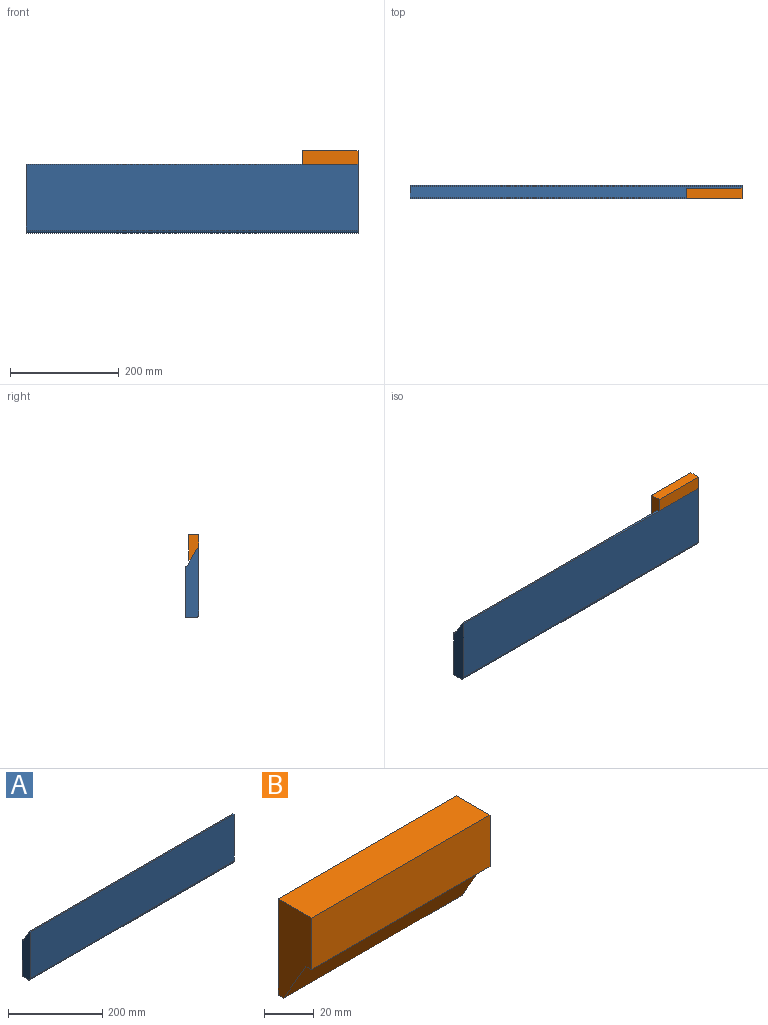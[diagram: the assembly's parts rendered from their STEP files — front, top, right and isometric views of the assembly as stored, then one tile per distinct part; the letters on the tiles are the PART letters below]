
ASSEMBLY  parts=2 mates=1
PART A: 9 faces, bbox 609.6x25.4x127 mm
  f0: plane 609.6x3.18mm, normal (0,0,1), area 1935.5mm2, adj f1,f6,f7,f8
  f1: plane 609.6x120.65mm, normal (0,-1,0), area 73548.2mm2, adj f0,f2,f7,f8
  f2: cylinder r=6.35mm len=609.6mm, axis (-1,0,0), area 6080.5mm2, adj f1,f3,f7,f8
  f3: plane 609.6x19.05mm, normal (0,0,-1), area 11612.9mm2, adj f2,f4,f7,f8
  f4: plane 609.6x94mm, normal (0,1,0), area 57305.1mm2, adj f3,f5,f7,f8
  f5: plane 609.6x3.18mm, normal (0,0,1), area 1935.5mm2, adj f4,f6,f7,f8
  f6: plane 609.6x33mm, normal (0,0.87,0.5), area 23225.8mm2, adj f0,f5,f7,f8
  f7: plane 127x25.4mm, normal (1,0,0), area 2798.1mm2, adj f0,f1,f2,f3,f4,f5,f6
  f8: plane 127x25.4mm, normal (-1,0,0), area 2798.1mm2, adj f0,f1,f2,f3,f4,f5,f6
PART B: 8 faces, bbox 101.6x19.1x47.4 mm
  f0: plane 101.6x25.4mm, normal (0,-1,0), area 2580.6mm2, adj f1,f5,f6,f7
  f1: plane 101.6x3.18mm, normal (0,0,-1), area 322.6mm2, adj f0,f2,f6,f7
  f2: plane 101.6x22mm, normal (0,-0.87,-0.5), area 2580.6mm2, adj f1,f3,f6,f7
  f3: plane 101.6x3.18mm, normal (0,0,-1), area 322.6mm2, adj f2,f4,f6,f7
  f4: plane 101.6x47.4mm, normal (0,1,0), area 4815.5mm2, adj f3,f5,f6,f7
  f5: plane 101.6x19.05mm, normal (0,0,1), area 1935.5mm2, adj f0,f4,f6,f7
  f6: plane 47.4x19.05mm, normal (1,0,0), area 693.4mm2, adj f0,f1,f2,f3,f4,f5
  f7: plane 47.4x19.05mm, normal (-1,0,0), area 693.4mm2, adj f0,f1,f2,f3,f4,f5
PLACE A at identity fixed
PLACE B t=(508,64.17,36.91)mm
MATE slider B.f6 <-> A.f7  axis (1,0,0) through (609.6,-44.31,103.54)mm
